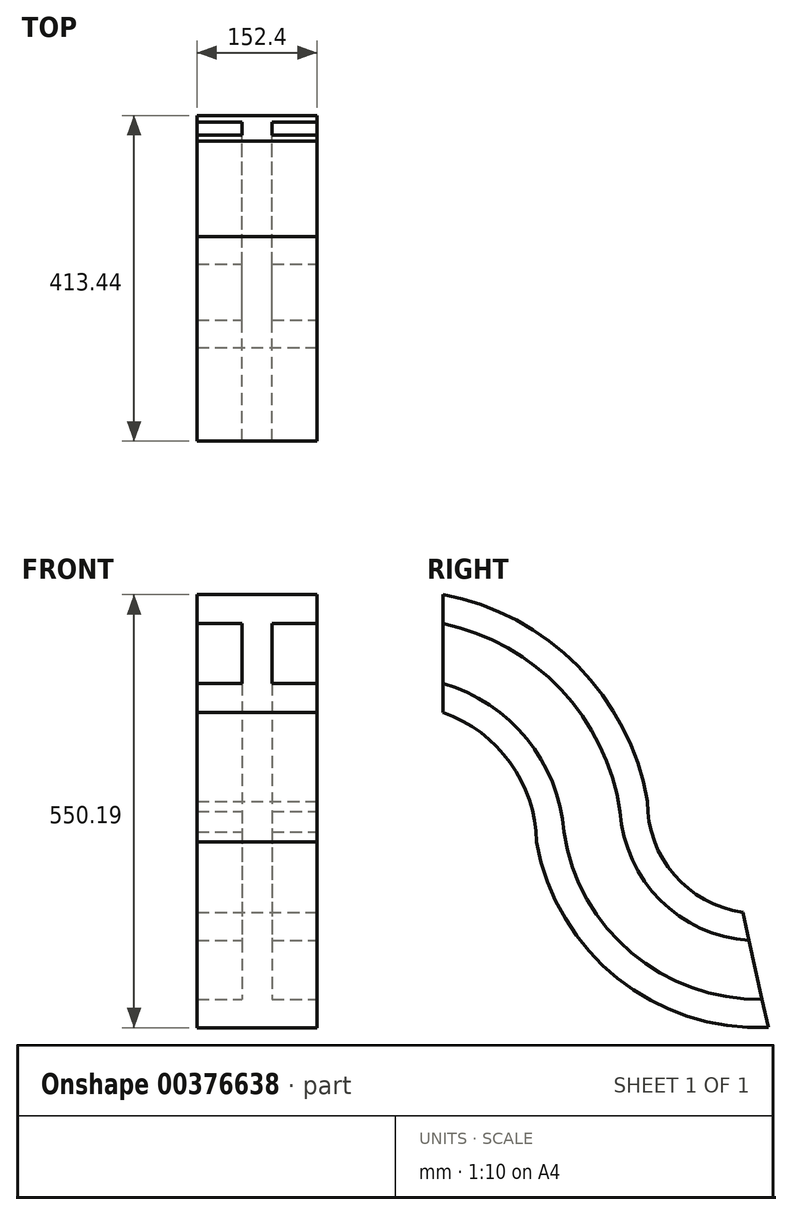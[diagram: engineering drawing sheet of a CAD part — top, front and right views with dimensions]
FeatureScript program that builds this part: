
annotation { "Feature Type Name" : "Feature", "Feature Type Description" : "" }
export const myFeature = defineFeature(function(context is Context, id is Id, definition is map)
    precondition{}
    {
        {
            var Q0;
            Q0=qCreatedBy(makeId("Front.planeOp"),FACE);
            var sketch = newSketch(context, id + "F0", { "sketchPlane" : qUnion([Q0])});
            skLineSegment(sketch, "E0.bottom", {"start": v(-76.2, 74.93) * mm, "end": v(76.2, 74.93) * mm});
            skLineSegment(sketch, "E0.top", {"start": v(-76.2, 38.1) * mm, "end": v(-19.05, 38.1) * mm});
            skLineSegment(sketch, "E0.left", {"start": v(-76.2, 74.93) * mm, "end": v(-76.2, 38.1) * mm});
            skLineSegment(sketch, "E0.right", {"start": v(76.2, 74.93) * mm, "end": v(76.2, 38.1) * mm});
            skLineSegment(sketch, "E1.bottom", {"start": v(-76.2, -74.93) * mm, "end": v(76.2, -74.93) * mm});
            skLineSegment(sketch, "E1.top", {"start": v(-76.2, -38.1) * mm, "end": v(-19.05, -38.1) * mm});
            skLineSegment(sketch, "E1.left", {"start": v(-76.2, -74.93) * mm, "end": v(-76.2, -38.1) * mm});
            skLineSegment(sketch, "E1.right", {"start": v(76.2, -74.93) * mm, "end": v(76.2, -38.1) * mm});
            skLineSegment(sketch, "E2.left", {"start": v(-19.05, 38.1) * mm, "end": v(-19.05, -38.1) * mm});
            skLineSegment(sketch, "E2.right", {"start": v(19.05, 38.1) * mm, "end": v(19.05, -38.1) * mm});
            skLineSegment(sketch, "E3.trimOffspring", {"start": v(19.05, 38.1) * mm, "end": v(76.2, 38.1) * mm});
            skLineSegment(sketch, "E4.trimOffspring", {"start": v(19.05, -38.1) * mm, "end": v(76.2, -38.1) * mm});
            skSolve(sketch);
        }
        {
            var Q0;
            Q0=qCreatedBy(makeId("Right.planeOp"),FACE);
            var sketch = newSketch(context, id + "F1", { "sketchPlane" : qUnion([Q0])});
            skArc(sketch, "E5", {"start": v(189.33, -213.6) * mm, "mid": v(128.28, -77) * mm, "end": v(0, 0) * mm});
            skArc(sketch, "E6", {"start": v(189.33, -213.6) * mm, "mid": v(257.84, -346.8) * mm, "end": v(397.15, -401.84) * mm});
            skSolve(sketch);
        }
        {
            var Q0;
            Q0=makeQuery(id+"F0.imprint","IMPRINT",FACE,{"disambiguationData":[TD([[makeQuery(id+"F0.imprint","IMPRINT",EDGE,{"derivedFrom":sQuery(id+"F0.wireOp",EDGE,"E0.bottom")}),-1.0]])]});
            var Q1;
            Q1 = qSketchRegion(id + "F1", true);
            var Q2;
            Q2 = qConstructionFilter(qBodyType(qCreatedBy(id + "F1" ,EDGE), BodyType.WIRE), ConstructionObject.NO);
            sweep(context, id + "F2", {"profiles" : qUnion([Q0, Q1]), "path" : qUnion([Q2])});
        }
    });
